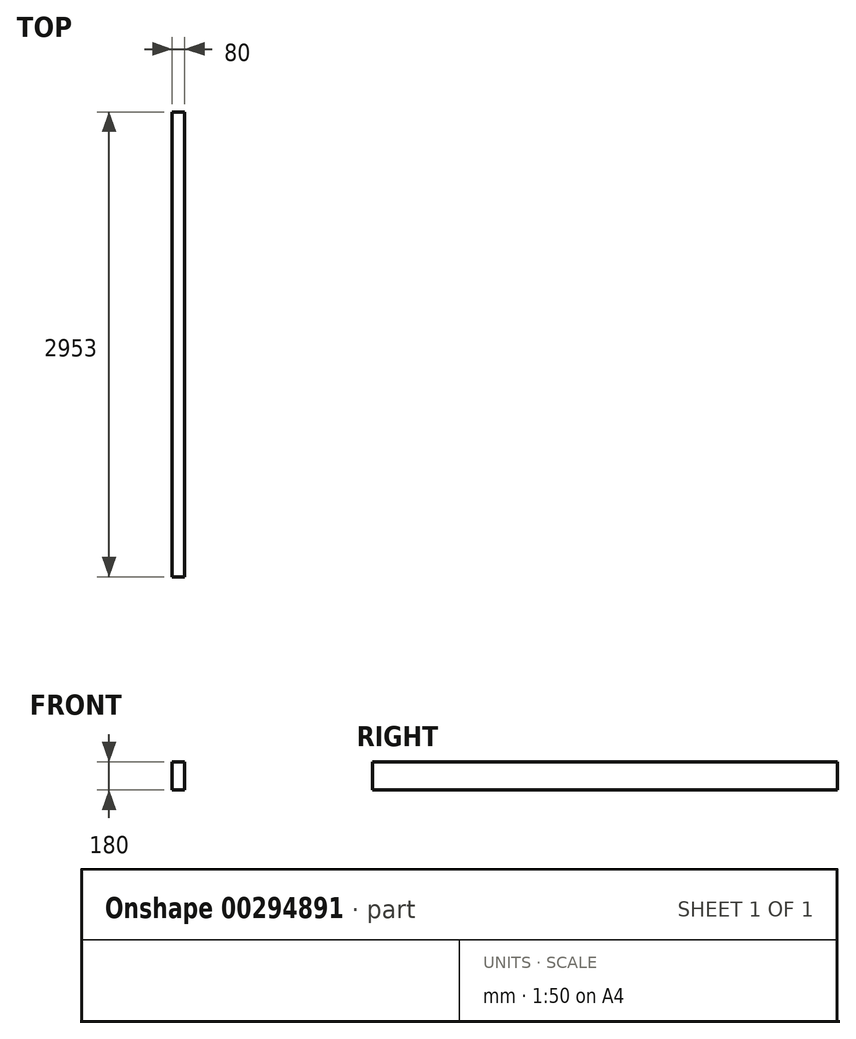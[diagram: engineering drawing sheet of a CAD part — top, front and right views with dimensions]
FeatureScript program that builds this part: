
annotation { "Feature Type Name" : "Feature", "Feature Type Description" : "" }
export const myFeature = defineFeature(function(context is Context, id is Id, definition is map)
    precondition{}
    {
        {
            var Q0;
            Q0=qCreatedBy(makeId("Front.planeOp"),FACE);
            var sketch = newSketch(context, id + "F0", { "sketchPlane" : qUnion([Q0])});
            skLineSegment(sketch, "E0.bottom", {"start": v(40, 90) * mm, "end": v(-40, 90) * mm});
            skLineSegment(sketch, "E0.top", {"start": v(40, -90) * mm, "end": v(-40, -90) * mm});
            skLineSegment(sketch, "E0.left", {"start": v(40, 90) * mm, "end": v(40, -90) * mm});
            skLineSegment(sketch, "E0.right", {"start": v(-40, 90) * mm, "end": v(-40, -90) * mm});
            skPoint(sketch, "E0.middle", {"position": v(0, 0) * mm});
            skSolve(sketch);
        }
        {
            var Q0;
            Q0 = qSketchRegion(id + "F0", true);
            extrude(context, id + "F1", {"entities" : qUnion([Q0]), "depth" : (3000 - 47) * mm});
        }
    });
